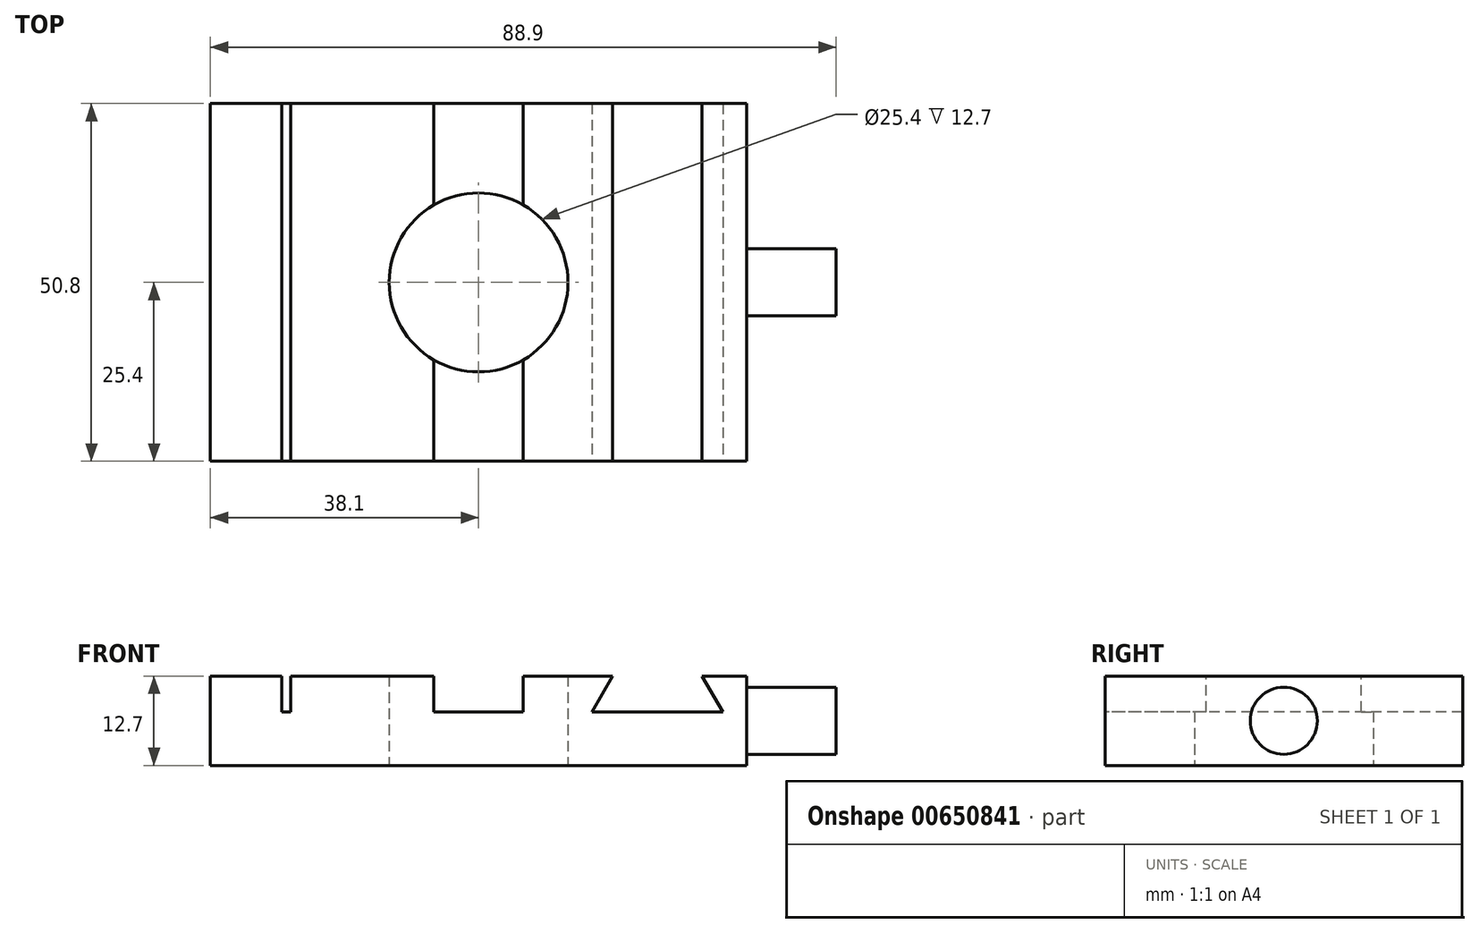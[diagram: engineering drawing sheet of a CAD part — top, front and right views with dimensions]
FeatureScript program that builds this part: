
annotation { "Feature Type Name" : "Feature", "Feature Type Description" : "" }
export const myFeature = defineFeature(function(context is Context, id is Id, definition is map)
    precondition{}
    {
        {
            var Q0;
            Q0=qCreatedBy(makeId("Top.planeOp"),FACE);
            var sketch = newSketch(context, id + "F0", { "sketchPlane" : qUnion([Q0])});
            skLineSegment(sketch, "E0.bottom", {"start": v(-38.1, 25.4) * mm, "end": v(38.1, 25.4) * mm});
            skLineSegment(sketch, "E0.top", {"start": v(-38.1, -25.4) * mm, "end": v(38.1, -25.4) * mm});
            skLineSegment(sketch, "E0.left", {"start": v(-38.1, 25.4) * mm, "end": v(-38.1, -25.4) * mm});
            skLineSegment(sketch, "E0.right", {"start": v(38.1, 25.4) * mm, "end": v(38.1, -25.4) * mm});
            skPoint(sketch, "E0.middle", {"position": v(0, 0) * mm});
            skCircle(sketch, "E1", {"center": v(0, 0) * mm, "radius": 12.7 * mm});
            skSolve(sketch);
        }
        {
            var Q0;
            Q0=makeQuery(id+"F0.imprint","IMPRINT",FACE,{"disambiguationData":[TD([[makeQuery(id+"F0.imprint","IMPRINT",EDGE,{"derivedFrom":sQuery(id+"F0.wireOp",EDGE,"E0.bottom")}),-1.0]])]});
            extrude(context, id + "F1", {"entities" : qUnion([Q0]), "depth" : 12.7 * mm, "offsetDistance" : 25.4 * mm});
        }
        {
            var Q0;
            Q0=makeQuery(id+"F1.opExtrude","CAP_FACE",FACE,{"disambiguationData":[OSD([sQuery(id+"F0.wireOp",EDGE,"E0.bottom"),sQuery(id+"F0.wireOp",EDGE,"E0.top"),sQuery(id+"F0.wireOp",EDGE,"E0.left"),sQuery(id+"F0.wireOp",EDGE,"E0.right"),sQuery(id+"F0.wireOp",EDGE,"E1")])],"isStart":false});
            var sketch = newSketch(context, id + "F2", { "sketchPlane" : qUnion([Q0])});
            skLineSegment(sketch, "E2.bottom", {"start": v(-27.94, 25.4) * mm, "end": v(-26.67, 25.4) * mm});
            skLineSegment(sketch, "E2.top", {"start": v(-27.94, -25.4) * mm, "end": v(-26.67, -25.4) * mm});
            skLineSegment(sketch, "E2.left", {"start": v(-27.94, 25.4) * mm, "end": v(-27.94, -25.4) * mm});
            skLineSegment(sketch, "E2.right", {"start": v(-26.67, 25.4) * mm, "end": v(-26.67, -25.4) * mm});
            skLineSegment(sketch, "E3", {"start": v(-6.35, 25.4) * mm, "end": v(-6.35, -25.4) * mm});
            skLineSegment(sketch, "E4", {"start": v(-6.35, -25.4) * mm, "end": v(6.35, -25.4) * mm});
            skLineSegment(sketch, "E5", {"start": v(6.35, -25.4) * mm, "end": v(6.35, 25.4) * mm});
            skLineSegment(sketch, "E6", {"start": v(6.35, 25.4) * mm, "end": v(-6.35, 25.4) * mm});
            skPoint(sketch, "E7", {"position": v(0, 0) * mm});
            skLineSegment(sketch, "E8", {"start": v(0, 25.4) * mm, "end": v(0, -25.4) * mm, "construction": true});
            skSolve(sketch);
        }
        {
            var Q0;
            Q0=makeQuery(id+"F2.imprint","IMPRINT",FACE,{"disambiguationData":[TD([[makeQuery(id+"F2.imprint","IMPRINT",EDGE,{"derivedFrom":sQuery(id+"F2.wireOp",EDGE,"E2.bottom")}),-1.0]])]});
            var Q1;
            {var subQ0=sQuery(id+"F2.wireOp",EDGE,"E6");Q1=makeQuery(id+"F2.imprint","IMPRINT",FACE,{"disambiguationData":[TD([[makeQuery(id+"F2.imprint","IMPRINT",EDGE,{"derivedFrom":subQ0}),-1.0]])]});}
            var Q2;
            {var subQ0=sQuery(id+"F2.wireOp",EDGE,"E4");Q2=makeQuery(id+"F2.imprint","IMPRINT",FACE,{"disambiguationData":[TD([[makeQuery(id+"F2.imprint","IMPRINT",EDGE,{"derivedFrom":subQ0}),1.0]])]});}
            extrude(context, id + "F3", {"entities" : qUnion([Q0, Q1, Q2]), "operationType" : NewBodyOperationType.REMOVE, "oppositeDirection" : true, "depth" : 5.08 * mm, "offsetDistance" : 25.4 * mm});
        }
        {
            var Q0;
            Q0=makeQuery(id+"F1.opExtrude","SWEPT_FACE",FACE,{"disambiguationData":[OSD([sQuery(id+"F0.wireOp",EDGE,"E0.top")])]});
            var sketch = newSketch(context, id + "F4", { "sketchPlane" : qUnion([Q0])});
            skLineSegment(sketch, "E9", {"start": v(19.05, 12.7) * mm, "end": v(16.12, 7.62) * mm});
            skLineSegment(sketch, "E10", {"start": v(16.12, 7.62) * mm, "end": v(34.68, 7.62) * mm});
            skLineSegment(sketch, "E11", {"start": v(34.68, 7.62) * mm, "end": v(31.75, 12.7) * mm});
            skLineSegment(sketch, "E12", {"start": v(31.75, 12.7) * mm, "end": v(19.05, 12.7) * mm});
            skLineSegment(sketch, "E13", {"start": v(25.4, 7.62) * mm, "end": v(25.4, 12.7) * mm, "construction": true});
            skSolve(sketch);
        }
        {
            var Q0;
            Q0 = qSketchRegion(id + "F4", true);
            extrude(context, id + "F5", {"entities" : qUnion([Q0]), "operationType" : NewBodyOperationType.REMOVE, "endBound" : BoundingType.THROUGH_ALL, "oppositeDirection" : true, "depth" : 25.4 * mm, "offsetDistance" : 25.4 * mm});
        }
        {
            var Q0;
            Q0=makeQuery(id+"F1.opExtrude","SWEPT_FACE",FACE,{"disambiguationData":[OSD([sQuery(id+"F0.wireOp",EDGE,"E0.right")])]});
            var sketch = newSketch(context, id + "F6", { "sketchPlane" : qUnion([Q0])});
            skCircle(sketch, "E14", {"center": v(0, 6.35) * mm, "radius": 4.76 * mm});
            skPoint(sketch, "E14.centerSnap0", {"position": v(-25.4, 6.35) * mm});
            skPoint(sketch, "E14.centerSnap1", {"position": v(0, 12.7) * mm});
            skSolve(sketch);
        }
        {
            var Q0;
            Q0 = qSketchRegion(id + "F6", true);
            extrude(context, id + "F7", {"entities" : qUnion([Q0]), "operationType" : NewBodyOperationType.ADD, "depth" : 12.7 * mm, "offsetDistance" : 25.4 * mm});
        }
    });
